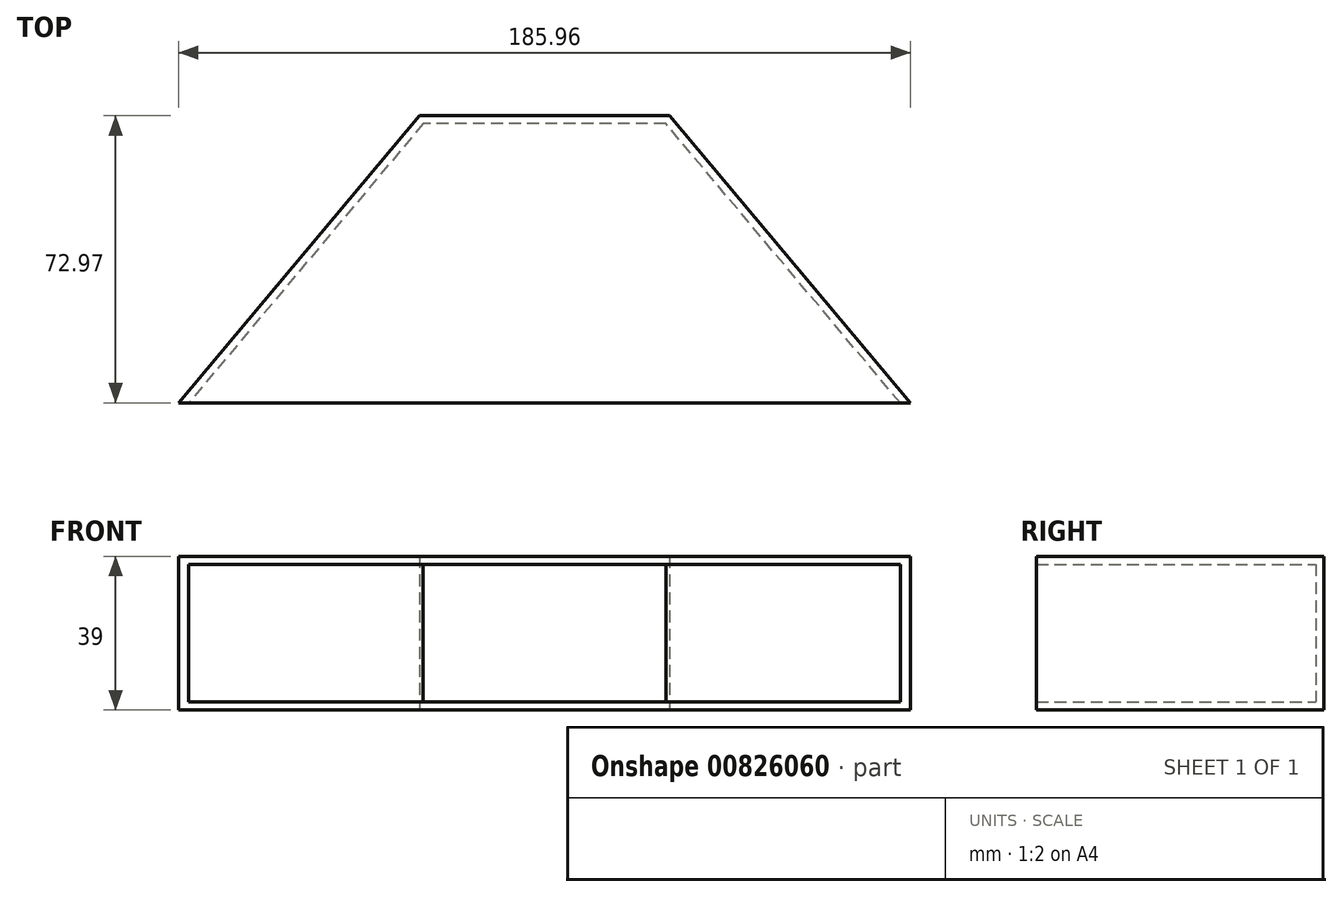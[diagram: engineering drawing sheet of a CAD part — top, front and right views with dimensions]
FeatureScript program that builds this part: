
annotation { "Feature Type Name" : "Feature", "Feature Type Description" : "" }
export const myFeature = defineFeature(function(context is Context, id is Id, definition is map)
    precondition{}
    {
        {
            var Q0;
            Q0=qCreatedBy(makeId("Top.planeOp"),FACE);
            var sketch = newSketch(context, id + "F0", { "sketchPlane" : qUnion([Q0])});
            skLineSegment(sketch, "E0", {"start": v(-92.98, 0) * mm, "end": v(92.98, 0) * mm});
            skLineSegment(sketch, "E1", {"start": v(31.75, 72.97) * mm, "end": v(-31.75, 72.97) * mm});
            skLineSegment(sketch, "E2", {"start": v(-31.75, 72.97) * mm, "end": v(-92.98, 0) * mm});
            skLineSegment(sketch, "E3", {"start": v(31.75, 72.97) * mm, "end": v(92.98, 0) * mm});
            skSolve(sketch);
        }
        {
            var Q0;
            Q0=makeQuery(id+"F0.imprint","IMPRINT",FACE,{"disambiguationData":[TD([[makeQuery(id+"F0.imprint","IMPRINT",EDGE,{"derivedFrom":sQuery(id+"F0.wireOp",EDGE,"E0")}),1.0]])]});
            extrude(context, id + "F1", {"entities" : qUnion([Q0]), "depth" : 2 * mm, "offsetDistance" : 25 * mm});
        }
        {
            var Q0;
            Q0=makeQuery(id+"F1.opExtrude","CAP_FACE",FACE,{"disambiguationData":[OSD([sQuery(id+"F0.wireOp",EDGE,"ovYM3qtu-96d5-KuZE-KJVZ-5yNf9sndBGPU"),sQuery(id+"F0.wireOp",EDGE,"klbATMvn-qYhZ-qeS5-bR5B-e85wnj71ZMQ5"),sQuery(id+"F0.wireOp",EDGE,"E0")])],"isStart":false});
            var sketch = newSketch(context, id + "F2", { "sketchPlane" : qUnion([Q0])});
            skLineSegment(sketch, "E4", {"start": v(90.36, 0) * mm, "end": v(30.82, 70.97) * mm});
            skLineSegment(sketch, "E5", {"start": v(30.82, 70.97) * mm, "end": v(-30.82, 70.97) * mm});
            skLineSegment(sketch, "E6", {"start": v(-30.82, 70.97) * mm, "end": v(-90.36, 0) * mm});
            skSolve(sketch);
        }
        {
            var Q0;
            {var subQ1=sQuery(id+"F2.wireOp",EDGE,"E4");Q0=makeQuery(id+"F2.imprint","IMPRINT",FACE,{"disambiguationData":[TD([[makeQuery(id+"F2.imprint","IMPRINT",EDGE,{"derivedFrom":subQ1}),-1.0]])]});}
            extrude(context, id + "F3", {"entities" : qUnion([Q0]), "operationType" : NewBodyOperationType.ADD, "depth" : 35 * mm, "offsetDistance" : 25 * mm});
        }
        {
            var Q0;
            Q0=makeQuery(id+"F3.opExtrude","CAP_FACE",FACE,{"disambiguationData":[OSD([sQuery(id+"F0.wireOp",EDGE,"ovYM3qtu-96d5-KuZE-KJVZ-5yNf9sndBGPU"),sQuery(id+"F0.wireOp",EDGE,"klbATMvn-qYhZ-qeS5-bR5B-e85wnj71ZMQ5"),sQuery(id+"F0.wireOp",EDGE,"E0"),sQuery(id+"F2.wireOp",EDGE,"NUnaVFQ4-v4Pk-x5QR-oLOL-oVXQoWjbFFwn"),sQuery(id+"F2.wireOp",EDGE,"z2io7HPl-rUTm-qE0x-gBUP-ijMSc0DEi6jP")])],"isStart":false});
            var sketch = newSketch(context, id + "F4", { "sketchPlane" : qUnion([Q0])});
            skLineSegment(sketch, "E7", {"start": v(-92.98, 0) * mm, "end": v(-31.75, 72.97) * mm});
            skLineSegment(sketch, "E8", {"start": v(-31.75, 72.97) * mm, "end": v(31.75, 72.97) * mm});
            skLineSegment(sketch, "E9", {"start": v(31.75, 72.97) * mm, "end": v(92.98, 0) * mm});
            skLineSegment(sketch, "E10", {"start": v(92.98, 0) * mm, "end": v(-92.98, 0) * mm});
            skSolve(sketch);
        }
        {
            var Q0;
            Q0 = qSketchRegion(id + "F4", true);
            var Q1;
            {var subQ1=makeQuery(id+"F3.opExtrude","CAP_EDGE",EDGE,{"disambiguationData":[OSD([sQuery(id+"F2.wireOp",EDGE,"NUnaVFQ4-v4Pk-x5QR-oLOL-oVXQoWjbFFwn")])],"isStart":false});Q1=makeQuery(id+"F4.imprint","IMPRINT",FACE,{"disambiguationData":[TD([[makeQuery(id+"F4.imprint","IMPRINT",EDGE,{"derivedFrom":subQ1}),-1.0]])]});}
            var Q2;
            {var subQ1=makeQuery(id+"F3.opExtrude","CAP_EDGE",EDGE,{"disambiguationData":[OSD([sQuery(id+"F2.wireOp",EDGE,"NUnaVFQ4-v4Pk-x5QR-oLOL-oVXQoWjbFFwn")])],"isStart":false});Q2=makeQuery(id+"F4.imprint","IMPRINT",FACE,{"disambiguationData":[TD([[makeQuery(id+"F4.imprint","IMPRINT",EDGE,{"derivedFrom":subQ1}),1.0]])]});}
            extrude(context, id + "F5", {"entities" : qUnion([Q0, Q1, Q2]), "operationType" : NewBodyOperationType.ADD, "depth" : 2 * mm, "offsetDistance" : 25 * mm});
        }
    });
